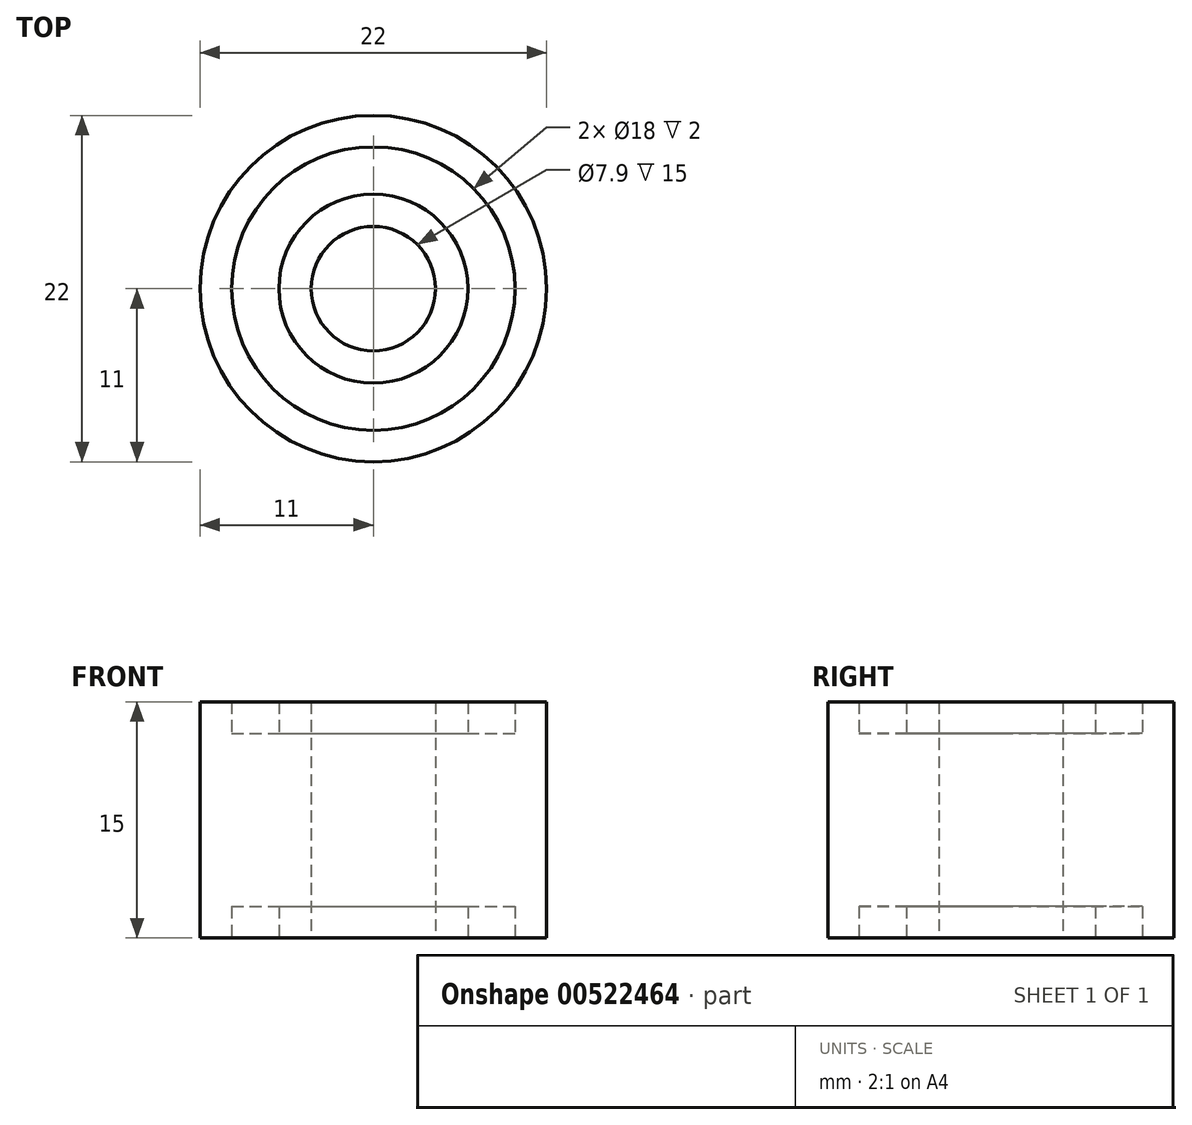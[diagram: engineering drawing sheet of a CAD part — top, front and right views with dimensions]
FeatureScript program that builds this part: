
annotation { "Feature Type Name" : "Feature", "Feature Type Description" : "" }
export const myFeature = defineFeature(function(context is Context, id is Id, definition is map)
    precondition{}
    {
        {
            var Q0;
            Q0=qCreatedBy(makeId("Front.planeOp"),FACE);
            var sketch = newSketch(context, id + "F0", { "sketchPlane" : qUnion([Q0])});
            skLineSegment(sketch, "E0.bottom", {"start": v(0, -7.5) * mm, "end": v(-6, -7.5) * mm});
            skLineSegment(sketch, "E0.top", {"start": v(-3.95, 7.5) * mm, "end": v(-6, 7.5) * mm});
            skLineSegment(sketch, "E0.left", {"start": v(0, -7.5) * mm, "end": v(0, 7.5) * mm, "construction": true});
            skLineSegment(sketch, "E0.right", {"start": v(-11, -7.5) * mm, "end": v(-11, 7.5) * mm});
            skLineSegment(sketch, "E1.bottom", {"start": v(-11, 7.5) * mm, "end": v(-9, 7.5) * mm});
            skLineSegment(sketch, "E1.left", {"start": v(-11, 7.5) * mm, "end": v(-11, 5.5) * mm});
            skLineSegment(sketch, "E1.right", {"start": v(-9, 7.5) * mm, "end": v(-9, 5.5) * mm});
            skLineSegment(sketch, "E2.left", {"start": v(-3.95, 7.5) * mm, "end": v(-3.95, 5.5) * mm});
            skLineSegment(sketch, "E2.right", {"start": v(-6, 7.5) * mm, "end": v(-6, 5.5) * mm});
            skLineSegment(sketch, "E3", {"start": v(-9, 5.5) * mm, "end": v(-6, 5.5) * mm});
            skLineSegment(sketch, "E4", {"start": v(-9, -5.5) * mm, "end": v(-9, -7.5) * mm});
            skLineSegment(sketch, "E5", {"start": v(-6, -5.5) * mm, "end": v(-6, -7.5) * mm});
            skLineSegment(sketch, "E6", {"start": v(-3.95, 5.5) * mm, "end": v(-3.95, -7.5) * mm});
            skPoint(sketch, "E7", {"position": v(-9, -5.5) * mm});
            skPoint(sketch, "E8", {"position": v(-6, -5.5) * mm});
            skLineSegment(sketch, "E9", {"start": v(-6, -5.5) * mm, "end": v(-9, -5.5) * mm});
            skLineSegment(sketch, "E10.trimOffspring", {"start": v(-9, 7.5) * mm, "end": v(-11, 7.5) * mm});
            skLineSegment(sketch, "E11.trimOffspring", {"start": v(-9, -7.5) * mm, "end": v(-11, -7.5) * mm});
            skPoint(sketch, "E12.orphan", {"position": v(-3.95, -5.5) * mm});
            skLineSegment(sketch, "E13", {"start": v(-11, 5.5) * mm, "end": v(-3.95, 5.5) * mm, "construction": true});
            skLineSegment(sketch, "E14", {"start": v(-3.95, -5.5) * mm, "end": v(-11, -5.5) * mm, "construction": true});
            skPoint(sketch, "E15", {"position": v(0, 0) * mm});
            skSolve(sketch);
        }
        {
            var Q0;
            Q0=makeQuery(id+"F0.imprint","IMPRINT",FACE,{"disambiguationData":[TD([[makeQuery(id+"F0.imprint","IMPRINT",EDGE,{"derivedFrom":sQuery(id+"F0.wireOp",EDGE,"E0.top")}),1.0]])]});
            var Q1;
            Q1=sQuery(id+"F0.wireOp",EDGE,"E0.left");
            revolve(context, id + "F1", {"entities" : qUnion([Q0]), "axis" : qUnion([Q1]), "revolveType" : RevolveType.FULL});
        }
    });
